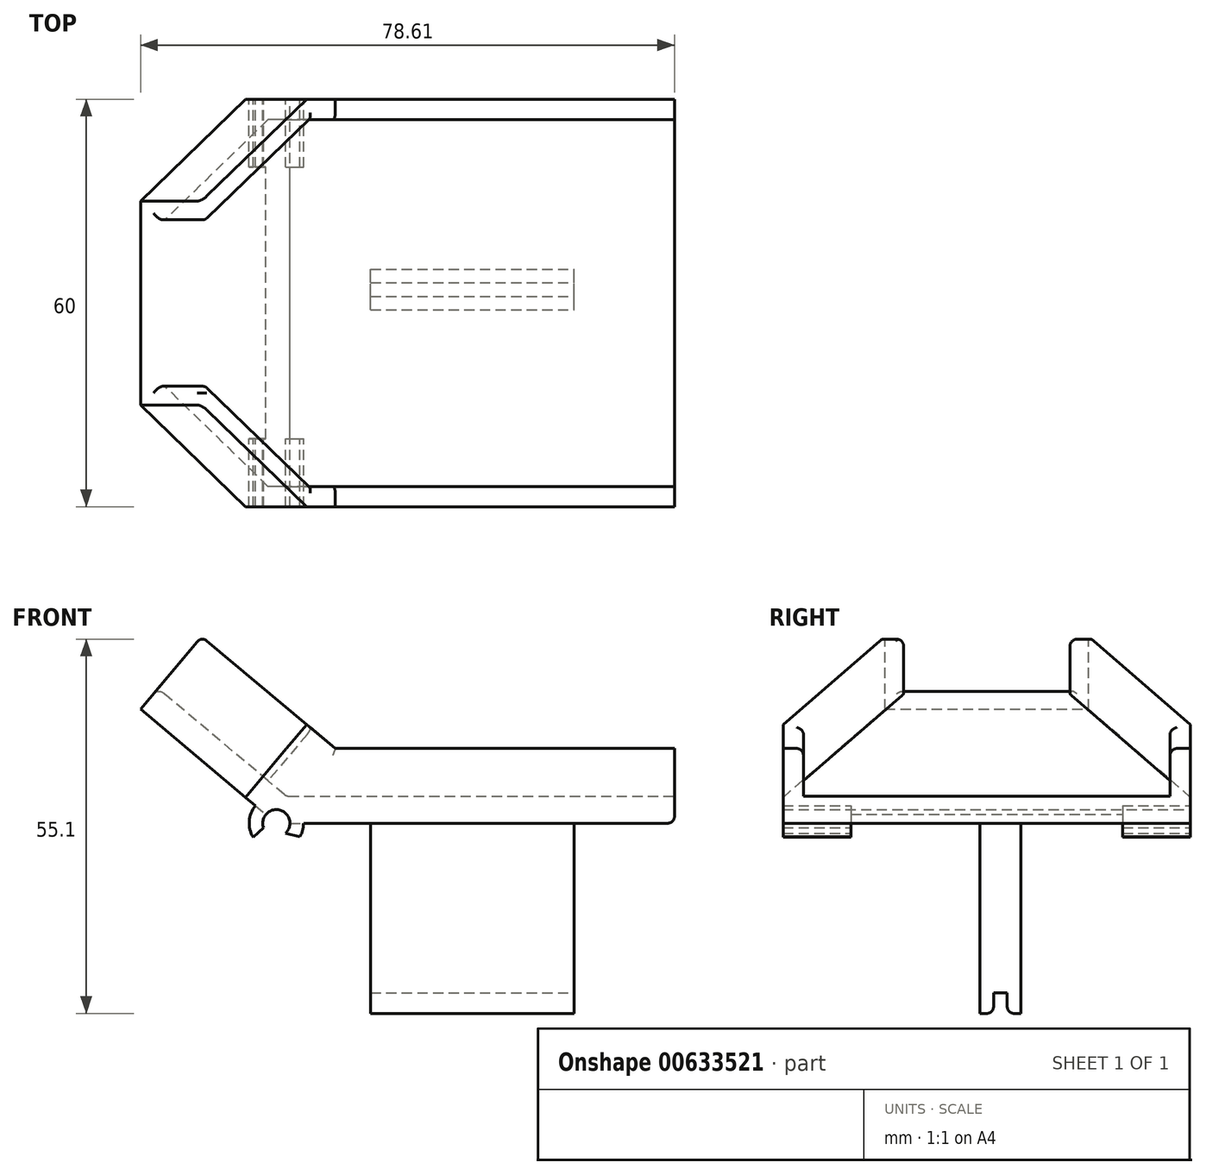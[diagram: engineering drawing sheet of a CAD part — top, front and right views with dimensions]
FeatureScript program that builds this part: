
annotation { "Feature Type Name" : "Feature", "Feature Type Description" : "" }
export const myFeature = defineFeature(function(context is Context, id is Id, definition is map)
    precondition{}
    {
        {
            var Q0;
            Q0=qCreatedBy(makeId("Front.planeOp"),FACE);
            var sketch = newSketch(context, id + "F0", { "sketchPlane" : qUnion([Q0])});
            skLineSegment(sketch, "E0.top", {"start": v(-24.08, 0) * mm, "end": v(33.08, 0) * mm});
            skLineSegment(sketch, "E0.right", {"start": v(33.08, -4) * mm, "end": v(33.08, 0) * mm});
            skLineSegment(sketch, "E1", {"start": v(-24.08, 0) * mm, "end": v(-42.96, 15.85) * mm});
            skLineSegment(sketch, "E2", {"start": v(-42.96, 15.85) * mm, "end": v(-45.53, 12.78) * mm});
            skLineSegment(sketch, "E3", {"start": v(-45.53, 12.78) * mm, "end": v(-28.6, -1.43) * mm});
            skArc(sketch, "E4", {"start": v(-24.17, -5.46) * mm, "mid": v(-25.06, -2.06) * mm, "end": v(-27.42, -4.67) * mm});
            skArc(sketch, "E5", {"start": v(-28.6, -1.43) * mm, "mid": v(-29.52, -3.7) * mm, "end": v(-28.95, -6.08) * mm});
            skLineSegment(sketch, "E6.trimOffspring", {"start": v(-21.53, -4) * mm, "end": v(33.08, -4) * mm});
            skLineSegment(sketch, "E7", {"start": v(-27.42, -4.67) * mm, "end": v(-28.95, -6.08) * mm});
            skLineSegment(sketch, "E8.MirrorCS", {"start": v(-24.17, -5.46) * mm, "end": v(-22.06, -5.99) * mm});
            skArc(sketch, "E9.MirrorCS", {"start": v(-21.53, -4) * mm, "mid": v(-21.67, -5.03) * mm, "end": v(-22.06, -5.99) * mm});
            skArc(sketch, "E10.trimOffspring", {"start": v(-28.95, -6.08) * mm, "mid": v(-29.38, -5.08) * mm, "end": v(-29.53, -4) * mm});
            skArc(sketch, "E11.trimOffspring", {"start": v(-22.06, -5.99) * mm, "mid": v(-21.67, -5.03) * mm, "end": v(-21.53, -4) * mm});
            skSolve(sketch);
        }
        {
            var Q0;
            Q0=makeQuery(id+"F0.imprint","IMPRINT",FACE,{"disambiguationData":[TD([[makeQuery(id+"F0.imprint","IMPRINT",EDGE,{"derivedFrom":sQuery(id+"F0.wireOp",EDGE,"E0.top")}),-1.0]])]});
            extrude(context, id + "F1", {"entities" : qUnion([Q0]), "depth" : 30 * mm, "offsetDistance" : 25 * mm, "hasSecondDirection" : true, "secondDirectionOppositeDirection" : true, "secondDirectionDepth" : 30 * mm});
        }
        {
            var Q0;
            Q0=qCreatedBy(makeId("Front.planeOp"),FACE);
            var sketch = newSketch(context, id + "F2", { "sketchPlane" : qUnion([Q0])});
            skLineSegment(sketch, "E12", {"start": v(-29.9, -0.33) * mm, "end": v(-25.52, -4) * mm});
            skLineSegment(sketch, "E13", {"start": v(-25.52, -4) * mm, "end": v(-20.66, -4) * mm});
            skLineSegment(sketch, "E14", {"start": v(-20.66, -4) * mm, "end": v(-20.66, -6.69) * mm});
            skLineSegment(sketch, "E15", {"start": v(-20.66, -6.69) * mm, "end": v(-30.15, -6.69) * mm});
            skLineSegment(sketch, "E16", {"start": v(-30.15, -6.69) * mm, "end": v(-29.9, -0.33) * mm});
            skSolve(sketch);
        }
        {
            var Q0;
            Q0=makeQuery(id+"F2.imprint","IMPRINT",FACE,{"disambiguationData":[TD([[makeQuery(id+"F2.imprint","IMPRINT",EDGE,{"derivedFrom":sQuery(id+"F2.wireOp",EDGE,"E12")}),-1.0]])]});
            extrude(context, id + "F3", {"entities" : qUnion([Q0]), "operationType" : NewBodyOperationType.REMOVE, "depth" : 20 * mm, "offsetDistance" : 25 * mm, "hasSecondDirection" : true, "secondDirectionOppositeDirection" : true, "secondDirectionDepth" : 20 * mm});
        }
        {
            var Q0;
            Q0=makeQuery(id+"F1.opExtrude","SWEPT_FACE",FACE,{"disambiguationData":[OSD([sQuery(id+"F0.wireOp",EDGE,"E1")])]});
            var sketch = newSketch(context, id + "F4", { "sketchPlane" : qUnion([Q0])});
            skLineSegment(sketch, "E17", {"start": v(-22.92, -30) * mm, "end": v(-43.1, -15) * mm});
            skLineSegment(sketch, "E18", {"start": v(-43.1, -15) * mm, "end": v(-43.1, -30) * mm});
            skLineSegment(sketch, "E19", {"start": v(-43.1, -30) * mm, "end": v(-22.92, -30) * mm});
            skLineSegment(sketch, "E20.MirrorCS", {"start": v(-43.1, 30) * mm, "end": v(-22.92, 30) * mm});
            skLineSegment(sketch, "E21.MirrorCS", {"start": v(-43.1, 15) * mm, "end": v(-43.1, 30) * mm});
            skLineSegment(sketch, "E22.MirrorCS", {"start": v(-22.92, 30) * mm, "end": v(-43.1, 15) * mm});
            skSolve(sketch);
        }
        {
            var Q0;
            Q0=makeQuery(id+"F4.imprint","IMPRINT",FACE,{"disambiguationData":[TD([[makeQuery(id+"F4.imprint","IMPRINT",EDGE,{"derivedFrom":sQuery(id+"F4.wireOp",EDGE,"E17")}),1.0]])]});
            var Q1;
            Q1=makeQuery(id+"F4.imprint","IMPRINT",FACE,{"disambiguationData":[TD([[makeQuery(id+"F4.imprint","IMPRINT",EDGE,{"derivedFrom":sQuery(id+"F4.wireOp",EDGE,"E20.MirrorCS")}),1.0]])]});
            extrude(context, id + "F5", {"entities" : qUnion([Q0, Q1]), "operationType" : NewBodyOperationType.REMOVE, "oppositeDirection" : true, "depth" : 25 * mm, "offsetDistance" : 25 * mm});
        }
        {
            var Q0;
            Q0=makeQuery(id+"F1.opExtrude","SWEPT_FACE",FACE,{"disambiguationData":[OSD([sQuery(id+"F0.wireOp",EDGE,"E1")])]});
            var sketch = newSketch(context, id + "F6", { "sketchPlane" : qUnion([Q0])});
            skLineSegment(sketch, "E23.0", {"start": v(-21.93, -27) * mm, "end": v(-43.1, -11.26) * mm});
            skLineSegment(sketch, "E23.1", {"start": v(-18.44, -27) * mm, "end": v(-21.93, -27) * mm});
            skLineSegment(sketch, "E24.MirrorCS", {"start": v(-21.93, 27) * mm, "end": v(-43.1, 11.26) * mm});
            skLineSegment(sketch, "E25.MirrorCS", {"start": v(-18.44, 27) * mm, "end": v(-21.93, 27) * mm});
            skSolve(sketch);
        }
        {
            var Q0;
            {var subQ4=sQuery(id+"F6.wireOp",EDGE,"E24.MirrorCS");Q0=makeQuery(id+"F6.imprint","IMPRINT",FACE,{"disambiguationData":[TD([[makeQuery(id+"F6.imprint","IMPRINT",EDGE,{"derivedFrom":subQ4}),-1.0]])]});}
            var Q1;
            {var subQ4=sQuery(id+"F6.wireOp",EDGE,"E23.0");Q1=makeQuery(id+"F6.imprint","IMPRINT",FACE,{"disambiguationData":[TD([[makeQuery(id+"F6.imprint","IMPRINT",EDGE,{"derivedFrom":subQ4}),1.0]])]});}
            extrude(context, id + "F7", {"entities" : qUnion([Q0, Q1]), "operationType" : NewBodyOperationType.ADD, "depth" : 10 * mm, "offsetDistance" : 25 * mm});
        }
        {
            var Q0;
            Q0=makeQuery(id+"F1.opExtrude","SWEPT_FACE",FACE,{"disambiguationData":[OSD([sQuery(id+"F0.wireOp",EDGE,"E0.top")])]});
            var sketch = newSketch(context, id + "F8", { "sketchPlane" : qUnion([Q0])});
            skLineSegment(sketch, "E26.0", {"start": v(-24.08, -27) * mm, "end": v(33.08, -27) * mm});
            skLineSegment(sketch, "E27.0", {"start": v(-24.08, 27) * mm, "end": v(33.08, 27) * mm});
            skSolve(sketch);
        }
        {
            var Q0;
            {var subQ0=sQuery(id+"F8.wireOp",EDGE,"E26.0");Q0=makeQuery(id+"F8.imprint","IMPRINT",FACE,{"disambiguationData":[TD([[makeQuery(id+"F8.imprint","IMPRINT",EDGE,{"derivedFrom":subQ0}),-1.0]])]});}
            var Q1;
            {var subQ0=sQuery(id+"F8.wireOp",EDGE,"E27.0");Q1=makeQuery(id+"F8.imprint","IMPRINT",FACE,{"disambiguationData":[TD([[makeQuery(id+"F8.imprint","IMPRINT",EDGE,{"derivedFrom":subQ0}),1.0]])]});}
            extrude(context, id + "F9", {"entities" : qUnion([Q0, Q1]), "operationType" : NewBodyOperationType.ADD, "depth" : 7 * mm, "offsetDistance" : 25 * mm});
        }
        {
            var Q0;
            {var subQ0=sQuery(id+"F0.wireOp",EDGE,"E1");var subQ1=sQuery(id+"F0.wireOp",EDGE,"E0.top");var subQ2=makeQuery(id+"F1.opExtrude","SWEPT_EDGE",EDGE,{"disambiguationData":[OSD([subQ1,subQ0])]});Q0=makeQuery(id+"F7.opExtrude","SWEPT_FACE",FACE,{"disambiguationData":[OSD([subQ1,subQ0]),TDD([makeQuery(id+"F6.imprint","IMPRINT",EDGE,{"disambiguationData":[TD([[makeQuery(id+"F6.imprint","INTERSECT",VERTEX,{"derivedFrom":[subQ2,makeQuery(id+"F1.opExtrude","CAP_EDGE",EDGE,{"disambiguationData":[OSD([subQ0])],"isStart":false})]}),-1.0]])],"derivedFrom":subQ2})])]});}
            extrude(context, id + "F10", {"entities" : qUnion([Q0]), "operationType" : NewBodyOperationType.ADD, "depth" : 5 * mm, "offsetDistance" : 25 * mm});
        }
        {
            var Q0;
            {var subQ0=sQuery(id+"F0.wireOp",EDGE,"E1");var subQ1=sQuery(id+"F0.wireOp",EDGE,"E0.top");var subQ2=makeQuery(id+"F1.opExtrude","SWEPT_EDGE",EDGE,{"disambiguationData":[OSD([subQ1,subQ0])]});Q0=makeQuery(id+"F7.opExtrude","SWEPT_FACE",FACE,{"disambiguationData":[OSD([subQ1,subQ0]),TDD([makeQuery(id+"F6.imprint","IMPRINT",EDGE,{"disambiguationData":[TD([[makeQuery(id+"F6.imprint","INTERSECT",VERTEX,{"derivedFrom":[subQ2,makeQuery(id+"F1.opExtrude","CAP_EDGE",EDGE,{"disambiguationData":[OSD([subQ0])],"isStart":true})]}),1.0]])],"derivedFrom":subQ2})])]});}
            extrude(context, id + "F11", {"entities" : qUnion([Q0]), "operationType" : NewBodyOperationType.ADD, "depth" : 5 * mm, "offsetDistance" : 25 * mm});
        }
        {
            var Q0;
            Q0=makeQuery(id+"F0.imprint","IMPRINT",FACE,{"disambiguationData":[TD([[makeQuery(id+"F0.imprint","IMPRINT",EDGE,{"derivedFrom":sQuery(id+"F0.wireOp",EDGE,"E0.top")}),-1.0]])]});
            var sketch = newSketch(context, id + "F12", { "sketchPlane" : qUnion([Q0])});
            skLineSegment(sketch, "E28", {"start": v(-8.66, -4) * mm, "end": v(7.52, -1.68) * mm});
            skLineSegment(sketch, "E29", {"start": v(7.52, -1.68) * mm, "end": v(7.86, -4) * mm});
            skLineSegment(sketch, "E30", {"start": v(7.86, -4) * mm, "end": v(-8.66, -4) * mm});
            skSolve(sketch);
        }
        {
            var Q0;
            Q0=makeQuery(id+"F1.opExtrude","SWEPT_FACE",FACE,{"disambiguationData":[OSD([sQuery(id+"F0.wireOp",EDGE,"E6.trimOffspring")])]});
            var sketch = newSketch(context, id + "F13", { "sketchPlane" : qUnion([Q0])});
            skSolve(sketch);
        }
        {
            var Q0;
            {var subQ5=sQuery(id+"F0.wireOp",EDGE,"E6.trimOffspring");Q0=makeQuery(id+"F13.imprint","IMPRINT",FACE,{"disambiguationData":[TD([[makeQuery(id+"F13.imprint","IMPRINT",EDGE,{"derivedFrom":makeQuery(id+"F1.opExtrude","CAP_EDGE",EDGE,{"disambiguationData":[OSD([subQ5])],"isStart":true})}),1.0]])]});}
            var sketch = newSketch(context, id + "F14", { "sketchPlane" : qUnion([Q0])});
            skLineSegment(sketch, "E31.bottom", {"start": v(-11.66, 1) * mm, "end": v(18.34, 1) * mm});
            skLineSegment(sketch, "E31.top", {"start": v(-11.66, -5) * mm, "end": v(18.34, -5) * mm});
            skLineSegment(sketch, "E31.left", {"start": v(-11.66, 1) * mm, "end": v(-11.66, -5) * mm});
            skLineSegment(sketch, "E31.right", {"start": v(18.34, 1) * mm, "end": v(18.34, -5) * mm});
            skSolve(sketch);
        }
        {
            var Q0;
            Q0=makeQuery(id+"F14.imprint","IMPRINT",FACE,{"disambiguationData":[TD([[makeQuery(id+"F14.imprint","IMPRINT",EDGE,{"derivedFrom":sQuery(id+"F14.wireOp",EDGE,"E31.bottom")}),-1.0]])]});
            extrude(context, id + "F15", {"entities" : qUnion([Q0]), "operationType" : NewBodyOperationType.ADD, "depth" : 25 * mm, "offsetDistance" : 25 * mm});
        }
        {
            var Q0;
            Q0=makeQuery(id+"F15.opExtrude","CAP_FACE",FACE,{"disambiguationData":[OSD([sQuery(id+"F14.wireOp",EDGE,"E31.bottom"),sQuery(id+"F14.wireOp",EDGE,"E31.top"),sQuery(id+"F14.wireOp",EDGE,"E31.left"),sQuery(id+"F14.wireOp",EDGE,"E31.right")])],"isStart":false});
            var sketch = newSketch(context, id + "F16", { "sketchPlane" : qUnion([Q0])});
            skLineSegment(sketch, "E32.0", {"start": v(-11.66, -3) * mm, "end": v(18.34, -3) * mm});
            skLineSegment(sketch, "E33.0", {"start": v(-11.66, -1) * mm, "end": v(18.34, -1) * mm});
            skSolve(sketch);
        }
        {
            var Q0;
            {var subQ0=sQuery(id+"F16.wireOp",EDGE,"E32.0");Q0=makeQuery(id+"F16.imprint","IMPRINT",FACE,{"disambiguationData":[TD([[makeQuery(id+"F16.imprint","IMPRINT",EDGE,{"derivedFrom":subQ0}),-1.0]])]});}
            var Q1;
            {var subQ0=sQuery(id+"F16.wireOp",EDGE,"E33.0");Q1=makeQuery(id+"F16.imprint","IMPRINT",FACE,{"disambiguationData":[TD([[makeQuery(id+"F16.imprint","IMPRINT",EDGE,{"derivedFrom":subQ0}),1.0]])]});}
            extrude(context, id + "F17", {"entities" : qUnion([Q0, Q1]), "operationType" : NewBodyOperationType.ADD, "depth" : 3 * mm, "offsetDistance" : 25 * mm});
        }
        {
            var Q0;
            Q0=makeQuery(id+"F17.opExtrude","CAP_EDGE",EDGE,{"disambiguationData":[OSD([sQuery(id+"F16.wireOp",EDGE,"E33.0")])],"isStart":false});
            var Q1;
            Q1=makeQuery(id+"F17.opExtrude","CAP_EDGE",EDGE,{"disambiguationData":[OSD([sQuery(id+"F16.wireOp",EDGE,"E32.0")])],"isStart":false});
            var Q2;
            Q2=makeQuery(id+"F1.opExtrude","SWEPT_EDGE",EDGE,{"disambiguationData":[OSD([sQuery(id+"F0.wireOp",EDGE,"E0.right"),sQuery(id+"F0.wireOp",EDGE,"E6.trimOffspring")])]});
            var Q3;
            Q3=makeQuery(id+"F9.opExtrude","CAP_EDGE",EDGE,{"disambiguationData":[OSD([sQuery(id+"F8.wireOp",EDGE,"E27.0")])],"isStart":false});
            var Q4;
            {var subQ0=sQuery(id+"F6.wireOp",EDGE,"E25.MirrorCS");Q4=makeQuery(id+"F11.boolean.opBoolean","MERGE",EDGE,{"derivedFrom":[makeQuery(id+"F7.opExtrude","CAP_EDGE",EDGE,{"disambiguationData":[OSD([subQ0])],"isStart":false}),makeQuery(id+"F11.opExtrude","SWEPT_EDGE",EDGE,{"disambiguationData":[OSD([sQuery(id+"F0.wireOp",EDGE,"E0.top"),sQuery(id+"F0.wireOp",EDGE,"E1"),subQ0])]})]});}
            var Q5;
            Q5=makeQuery(id+"F7.opExtrude","CAP_EDGE",EDGE,{"disambiguationData":[OSD([sQuery(id+"F6.wireOp",EDGE,"E24.MirrorCS")])],"isStart":false});
            var Q6;
            {var subQ0=sQuery(id+"F0.wireOp",EDGE,"E2");var subQ1=sQuery(id+"F0.wireOp",EDGE,"E1");var subQ2=makeQuery(id+"F1.opExtrude","SWEPT_EDGE",EDGE,{"disambiguationData":[OSD([subQ1,subQ0])]});Q6=makeQuery(id+"F7.opExtrude","CAP_EDGE",EDGE,{"disambiguationData":[OSD([subQ1,subQ0]),TDD([makeQuery(id+"F6.imprint","IMPRINT",EDGE,{"disambiguationData":[TD([[makeQuery(id+"F6.imprint","INTERSECT",VERTEX,{"derivedFrom":[makeQuery(id+"F5.boolean.opBoolean","COPY",EDGE,{"derivedFrom":makeQuery(id+"F5.opExtrude","CAP_EDGE",EDGE,{"disambiguationData":[OSD([sQuery(id+"F4.wireOp",EDGE,"E22.MirrorCS")])],"isStart":true})}),subQ2]}),1.0]])],"derivedFrom":subQ2})])],"isStart":false});}
            var Q7;
            {var subQ0=sQuery(id+"F0.wireOp",EDGE,"E2");var subQ1=sQuery(id+"F0.wireOp",EDGE,"E1");var subQ2=makeQuery(id+"F1.opExtrude","SWEPT_EDGE",EDGE,{"disambiguationData":[OSD([subQ1,subQ0])]});Q7=makeQuery(id+"F7.opExtrude","CAP_EDGE",EDGE,{"disambiguationData":[OSD([subQ1,subQ0]),TDD([makeQuery(id+"F6.imprint","IMPRINT",EDGE,{"disambiguationData":[TD([[makeQuery(id+"F6.imprint","INTERSECT",VERTEX,{"derivedFrom":[makeQuery(id+"F5.boolean.opBoolean","COPY",EDGE,{"derivedFrom":makeQuery(id+"F5.opExtrude","CAP_EDGE",EDGE,{"disambiguationData":[OSD([sQuery(id+"F4.wireOp",EDGE,"E17")])],"isStart":true})}),subQ2]}),-1.0]])],"derivedFrom":subQ2})])],"isStart":false});}
            var Q8;
            Q8=makeQuery(id+"F7.opExtrude","CAP_EDGE",EDGE,{"disambiguationData":[OSD([sQuery(id+"F6.wireOp",EDGE,"E23.0")])],"isStart":false});
            var Q9;
            {var subQ0=sQuery(id+"F6.wireOp",EDGE,"E23.1");Q9=makeQuery(id+"F10.boolean.opBoolean","MERGE",EDGE,{"derivedFrom":[makeQuery(id+"F7.opExtrude","CAP_EDGE",EDGE,{"disambiguationData":[OSD([subQ0])],"isStart":false}),makeQuery(id+"F10.opExtrude","SWEPT_EDGE",EDGE,{"disambiguationData":[OSD([sQuery(id+"F0.wireOp",EDGE,"E0.top"),sQuery(id+"F0.wireOp",EDGE,"E1"),subQ0])]})]});}
            var Q10;
            Q10=makeQuery(id+"F9.opExtrude","CAP_EDGE",EDGE,{"disambiguationData":[OSD([sQuery(id+"F8.wireOp",EDGE,"E26.0")])],"isStart":false});
            var Q11;
            Q11=makeQuery(id+"F7.opExtrude","SWEPT_EDGE",EDGE,{"disambiguationData":[OSD([sQuery(id+"F0.wireOp",EDGE,"E1"),sQuery(id+"F0.wireOp",EDGE,"E2"),sQuery(id+"F6.wireOp",EDGE,"E24.MirrorCS")])]});
            var Q12;
            Q12=makeQuery(id+"F7.opExtrude","SWEPT_EDGE",EDGE,{"disambiguationData":[OSD([sQuery(id+"F0.wireOp",EDGE,"E1"),sQuery(id+"F0.wireOp",EDGE,"E2"),sQuery(id+"F6.wireOp",EDGE,"E23.0")])]});
            var Q13;
            Q13=makeQuery(id+"F1.opExtrude","SWEPT_EDGE",EDGE,{"disambiguationData":[OSD([sQuery(id+"F0.wireOp",EDGE,"E1"),sQuery(id+"F0.wireOp",EDGE,"E2")])]});
            var Q14;
            Q14=makeQuery(id+"F7.boolean.opBoolean","SPLIT",EDGE,{"derivedFrom":makeQuery(id+"F1.opExtrude","SWEPT_EDGE",EDGE,{"disambiguationData":[OSD([sQuery(id+"F0.wireOp",EDGE,"E0.top"),sQuery(id+"F0.wireOp",EDGE,"E1")])]})});
            fillet(context, id + "F18", {"entities" : qUnion([Q0, Q1, Q2, Q3, Q4, Q5, Q6, Q7, Q8, Q9, Q10, Q11, Q12, Q13, Q14]), "radius" : 1 * mm, "tangentPropagation" : true, "allowEdgeOverflow" : false});
        }
    });
